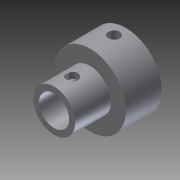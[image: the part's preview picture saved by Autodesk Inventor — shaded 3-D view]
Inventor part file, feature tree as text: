
AUTODESK INVENTOR PART (.ipt)
format: ipt  version: 2012 (Build 160160000, 160)  size: 117,760 bytes
history: native  units: in
note: dims shown in document units (in); Inventor stores cm internally (conversion verified against a paired STEP export)
features: extrude x4, sketch x2
ambient origin geometry x8: Origin, YZ Plane, XZ Plane, XY Plane, X Axis, Y Axis, Z Axis, Center Point
bodies: Solid1 (feature_tree)
feature tree (6):
  sketch  "Sketch1"  dims[d0=0.5625in d1=0.75in]
  extrude  "Extrusion1"  Depth=0.75in
  extrude  "Extrusion2"  Depth=0.4375in
  extrude  "Extrusion3"  Depth=0.125in TaperAngle=0.0deg
  extrude  "Extrusion4"  Depth=0.5in TaperAngle=0.0deg
  sketch  "Sketch2"  dims[d2=0.315in d3=0.4375in d4=0.125in d5=0.0in d6=0.5in d7=0.0in d8=0.25in d9=0.0in d10=0.1181in d11=0.125in d12=0.1875in d13=0.375in d14=0.0in]
